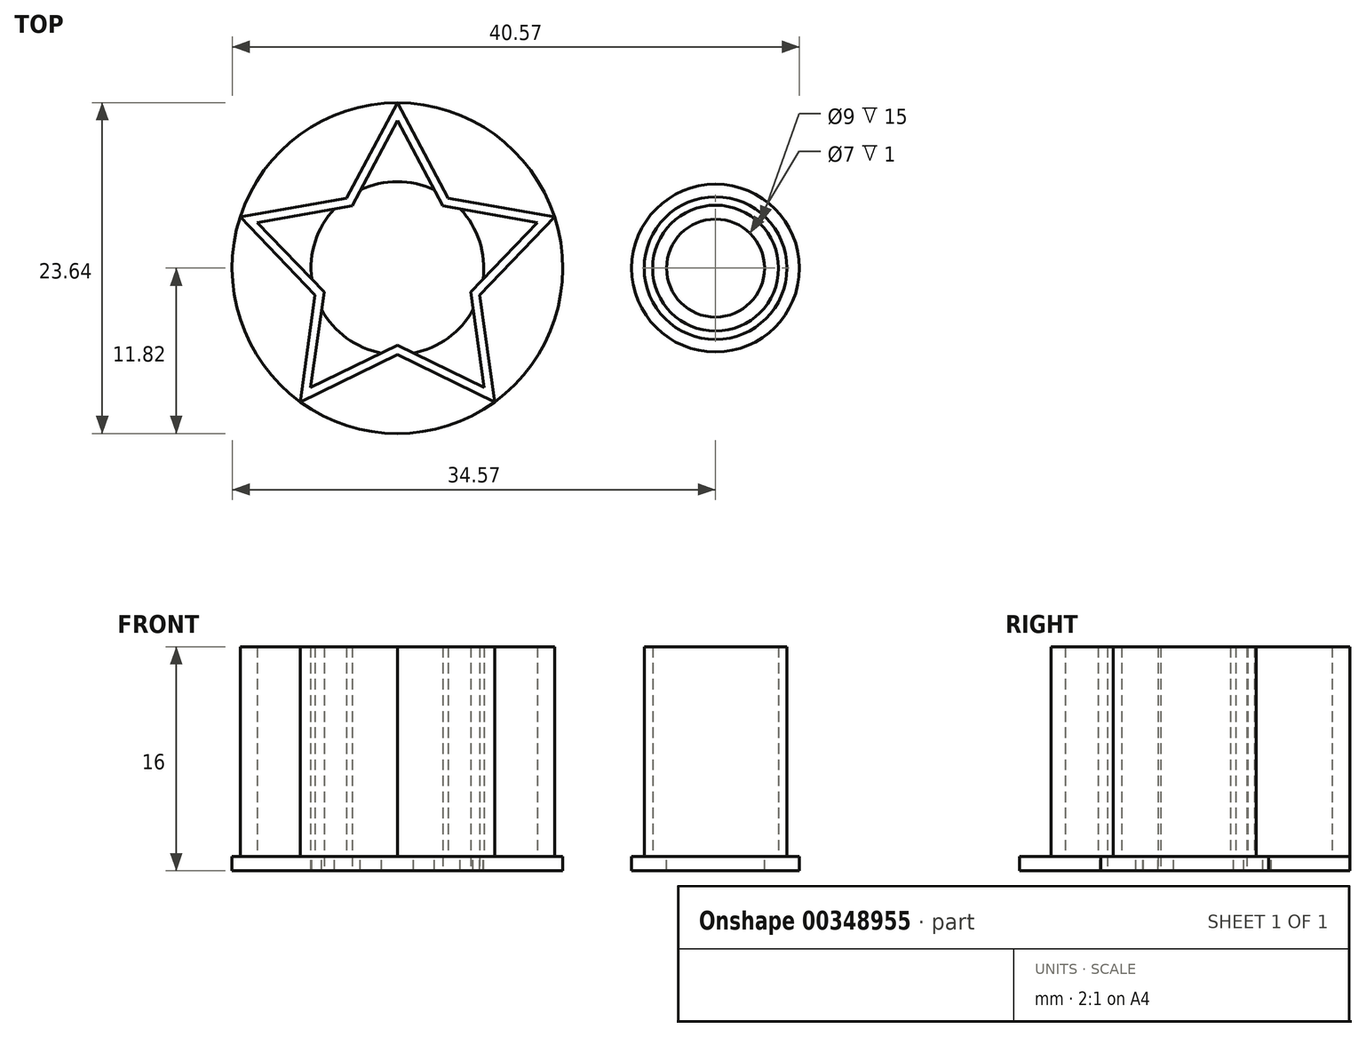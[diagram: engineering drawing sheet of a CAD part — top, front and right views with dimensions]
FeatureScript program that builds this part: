
annotation { "Feature Type Name" : "Feature", "Feature Type Description" : "" }
export const myFeature = defineFeature(function(context is Context, id is Id, definition is map)
    precondition{}
    {
        {
            var Q0;
            Q0=qCreatedBy(makeId("Top.planeOp"),FACE);
            var sketch = newSketch(context, id + "F0", { "sketchPlane" : qUnion([Q0])});
            skCircle(sketch, "E0", {"center": v(0, 0) * mm, "radius": 5.1 * mm});
            skCircle(sketch, "E1", {"center": v(0, 0) * mm, "radius": 4.5 * mm});
            skCircle(sketch, "E2", {"center": v(0, 0) * mm, "radius": 6 * mm});
            skCircle(sketch, "E3", {"center": v(0, 0) * mm, "radius": 3.5 * mm});
            skSolve(sketch);
        }
        {
            var Q0;
            Q0=makeQuery(id+"F0.imprint","IMPRINT",FACE,{"disambiguationData":[TD([[makeQuery(id+"F0.imprint","IMPRINT",EDGE,{"derivedFrom":sQuery(id+"F0.wireOp",EDGE,"E0")}),1.0]])]});
            extrude(context, id + "F1", {"entities" : qUnion([Q0]), "depth" : 15 * mm});
        }
        {
            var Q0;
            Q0=makeQuery(id+"F0.imprint","IMPRINT",FACE,{"disambiguationData":[TD([[makeQuery(id+"F0.imprint","IMPRINT",EDGE,{"derivedFrom":sQuery(id+"F0.wireOp",EDGE,"E0")}),-1.0]])]});
            var Q1;
            Q1=makeQuery(id+"F0.imprint","IMPRINT",FACE,{"disambiguationData":[TD([[makeQuery(id+"F0.imprint","IMPRINT",EDGE,{"derivedFrom":sQuery(id+"F0.wireOp",EDGE,"E1")}),1.0]])]});
            var Q2;
            Q2=makeQuery(id+"F0.imprint","IMPRINT",FACE,{"disambiguationData":[TD([[makeQuery(id+"F0.imprint","IMPRINT",EDGE,{"derivedFrom":sQuery(id+"F0.wireOp",EDGE,"E0")}),1.0]])]});
            extrude(context, id + "F2", {"entities" : qUnion([Q0, Q1, Q2]), "operationType" : NewBodyOperationType.ADD, "oppositeDirection" : true, "depth" : 1 * mm});
        }
        {
            var Q0;
            Q0=qCreatedBy(makeId("Top.planeOp"),FACE);
            var sketch = newSketch(context, id + "F3", { "sketchPlane" : qUnion([Q0])});
            skCircle(sketch, "E4.cCircle", {"center": v(-22.75, 0) * mm, "radius": 5 * mm, "construction": true});
            skLineSegment(sketch, "E4.0", {"start": v(-26.39, 5) * mm, "end": v(-19.12, 5) * mm});
            skLineSegment(sketch, "E4.1", {"start": v(-19.12, 5) * mm, "end": v(-16.88, -1.9) * mm});
            skLineSegment(sketch, "E4.2", {"start": v(-16.88, -1.9) * mm, "end": v(-22.75, -6.18) * mm});
            skLineSegment(sketch, "E4.3", {"start": v(-22.75, -6.18) * mm, "end": v(-28.63, -1.9) * mm});
            skLineSegment(sketch, "E4.4", {"start": v(-28.63, -1.9) * mm, "end": v(-26.39, 5) * mm});
            skPoint(sketch, "E4.0.midPoint", {"position": v(-22.75, 5) * mm});
            skLineSegment(sketch, "E5", {"start": v(-26.39, 5) * mm, "end": v(-34, 3.65) * mm});
            skLineSegment(sketch, "E6", {"start": v(-34, 3.65) * mm, "end": v(-28.63, -1.9) * mm});
            skLineSegment(sketch, "E7", {"start": v(-28.63, -1.9) * mm, "end": v(-29.7, -9.56) * mm});
            skLineSegment(sketch, "E8", {"start": v(-29.7, -9.56) * mm, "end": v(-22.75, -6.18) * mm});
            skLineSegment(sketch, "E9", {"start": v(-22.75, -6.18) * mm, "end": v(-15.8, -9.56) * mm});
            skLineSegment(sketch, "E10", {"start": v(-15.8, -9.56) * mm, "end": v(-16.88, -1.9) * mm});
            skLineSegment(sketch, "E11", {"start": v(-16.88, -1.9) * mm, "end": v(-11.51, 3.65) * mm});
            skLineSegment(sketch, "E12", {"start": v(-11.51, 3.65) * mm, "end": v(-19.12, 5) * mm});
            skLineSegment(sketch, "E13", {"start": v(-19.12, 5) * mm, "end": v(-22.75, 11.82) * mm});
            skLineSegment(sketch, "E14", {"start": v(-22.75, 11.82) * mm, "end": v(-26.39, 5) * mm});
            skSolve(sketch);
        }
        {
            var Q0;
            Q0 = qSketchRegion(id + "F3", true);
            extrude(context, id + "F4", {"entities" : qUnion([Q0]), "depth" : 15 * mm});
        }
        {
            var Q0;
            Q0=makeQuery(id+"F4.opExtrude","CAP_FACE",FACE,{"disambiguationData":[OSD([sQuery(id+"F3.wireOp",EDGE,"E5"),sQuery(id+"F3.wireOp",EDGE,"E6"),sQuery(id+"F3.wireOp",EDGE,"E7"),sQuery(id+"F3.wireOp",EDGE,"E8"),sQuery(id+"F3.wireOp",EDGE,"E9"),sQuery(id+"F3.wireOp",EDGE,"E10"),sQuery(id+"F3.wireOp",EDGE,"E11"),sQuery(id+"F3.wireOp",EDGE,"E12"),sQuery(id+"F3.wireOp",EDGE,"E13"),sQuery(id+"F3.wireOp",EDGE,"E14")])],"isStart":false});
            shell(context, id + "F5", {"entities" : qUnion([Q0]), "thickness" : 0.6 * mm});
        }
        {
            var Q0;
            Q0=makeQuery(id+"F5.opShell","OFFSET_FACE",FACE,{"disambiguationData":[OSD([sQuery(id+"F3.wireOp",EDGE,"E5"),sQuery(id+"F3.wireOp",EDGE,"E6"),sQuery(id+"F3.wireOp",EDGE,"E7"),sQuery(id+"F3.wireOp",EDGE,"E8"),sQuery(id+"F3.wireOp",EDGE,"E9"),sQuery(id+"F3.wireOp",EDGE,"E10"),sQuery(id+"F3.wireOp",EDGE,"E11"),sQuery(id+"F3.wireOp",EDGE,"E12"),sQuery(id+"F3.wireOp",EDGE,"E13"),sQuery(id+"F3.wireOp",EDGE,"E14")])]});
            extrude(context, id + "F6", {"entities" : qUnion([Q0]), "operationType" : NewBodyOperationType.REMOVE, "oppositeDirection" : true, "depth" : 25 * mm});
        }
        {
            var Q0;
            Q0=makeQuery(id+"F4.opExtrude","CAP_FACE",FACE,{"disambiguationData":[OSD([sQuery(id+"F3.wireOp",EDGE,"E5"),sQuery(id+"F3.wireOp",EDGE,"E6"),sQuery(id+"F3.wireOp",EDGE,"E7"),sQuery(id+"F3.wireOp",EDGE,"E8"),sQuery(id+"F3.wireOp",EDGE,"E9"),sQuery(id+"F3.wireOp",EDGE,"E10"),sQuery(id+"F3.wireOp",EDGE,"E11"),sQuery(id+"F3.wireOp",EDGE,"E12"),sQuery(id+"F3.wireOp",EDGE,"E13"),sQuery(id+"F3.wireOp",EDGE,"E14")])],"isStart":true});
            var sketch = newSketch(context, id + "F7", { "sketchPlane" : qUnion([Q0])});
            skCircle(sketch, "E15", {"center": v(-22.75, 0) * mm, "radius": 11.82 * mm});
            skCircle(sketch, "E16", {"center": v(-22.75, 0) * mm, "radius": 6.18 * mm});
            skSolve(sketch);
        }
        {
            var Q0;
            {var subQ7=makeQuery(id+"F4.opExtrude","CAP_EDGE",EDGE,{"disambiguationData":[OSD([sQuery(id+"F3.wireOp",EDGE,"E8")])],"isStart":true});Q0=makeQuery(id+"F7.imprint","IMPRINT",FACE,{"disambiguationData":[TD([[makeQuery(id+"F7.imprint","IMPRINT",EDGE,{"derivedFrom":subQ7}),1.0]])]});}
            var Q1;
            {var subQ0=sQuery(id+"F7.wireOp",EDGE,"E16");var subQ1=sQuery(id+"F3.wireOp",EDGE,"E10");var subQ2=sQuery(id+"F3.wireOp",EDGE,"E9");var subQ3=makeQuery(id+"F4.opExtrude","CAP_FACE",FACE,{"disambiguationData":[OSD([sQuery(id+"F3.wireOp",EDGE,"E5"),sQuery(id+"F3.wireOp",EDGE,"E6"),sQuery(id+"F3.wireOp",EDGE,"E7"),sQuery(id+"F3.wireOp",EDGE,"E8"),subQ2,subQ1,sQuery(id+"F3.wireOp",EDGE,"E11"),sQuery(id+"F3.wireOp",EDGE,"E12"),sQuery(id+"F3.wireOp",EDGE,"E13"),sQuery(id+"F3.wireOp",EDGE,"E14")])],"isStart":true});var subQ4=makeQuery(id+"F6.boolean.opBoolean","INTERSECT",EDGE,{"derivedFrom":[subQ3,makeQuery(id+"F6.opExtrude","SWEPT_FACE",FACE,{"disambiguationData":[OSD([subQ1])]})]});var subQ5=makeQuery(id+"F7.imprint","INTERSECT",VERTEX,{"derivedFrom":[subQ4,subQ0]});Q1=makeQuery(id+"F7.imprint","IMPRINT",FACE,{"disambiguationData":[TD([[makeQuery(id+"F7.imprint","IMPRINT",EDGE,{"disambiguationData":[TD([[subQ5,-1.0]])],"derivedFrom":subQ0}),-1.0]])]});}
            var Q2;
            {var subQ0=sQuery(id+"F7.wireOp",EDGE,"E16");var subQ1=sQuery(id+"F3.wireOp",EDGE,"E8");var subQ2=sQuery(id+"F3.wireOp",EDGE,"E7");var subQ3=makeQuery(id+"F4.opExtrude","CAP_FACE",FACE,{"disambiguationData":[OSD([sQuery(id+"F3.wireOp",EDGE,"E5"),sQuery(id+"F3.wireOp",EDGE,"E6"),subQ2,subQ1,sQuery(id+"F3.wireOp",EDGE,"E9"),sQuery(id+"F3.wireOp",EDGE,"E10"),sQuery(id+"F3.wireOp",EDGE,"E11"),sQuery(id+"F3.wireOp",EDGE,"E12"),sQuery(id+"F3.wireOp",EDGE,"E13"),sQuery(id+"F3.wireOp",EDGE,"E14")])],"isStart":true});var subQ4=makeQuery(id+"F6.boolean.opBoolean","INTERSECT",EDGE,{"derivedFrom":[subQ3,makeQuery(id+"F6.opExtrude","SWEPT_FACE",FACE,{"disambiguationData":[OSD([subQ1])]})]});var subQ5=makeQuery(id+"F7.imprint","INTERSECT",VERTEX,{"derivedFrom":[subQ4,subQ0]});Q2=makeQuery(id+"F7.imprint","IMPRINT",FACE,{"disambiguationData":[TD([[makeQuery(id+"F7.imprint","IMPRINT",EDGE,{"disambiguationData":[TD([[subQ5,-1.0]])],"derivedFrom":subQ0}),-1.0]])]});}
            var Q3;
            {var subQ0=sQuery(id+"F7.wireOp",EDGE,"E16");var subQ1=sQuery(id+"F3.wireOp",EDGE,"E6");var subQ2=sQuery(id+"F3.wireOp",EDGE,"E5");var subQ3=makeQuery(id+"F4.opExtrude","CAP_FACE",FACE,{"disambiguationData":[OSD([subQ2,subQ1,sQuery(id+"F3.wireOp",EDGE,"E7"),sQuery(id+"F3.wireOp",EDGE,"E8"),sQuery(id+"F3.wireOp",EDGE,"E9"),sQuery(id+"F3.wireOp",EDGE,"E10"),sQuery(id+"F3.wireOp",EDGE,"E11"),sQuery(id+"F3.wireOp",EDGE,"E12"),sQuery(id+"F3.wireOp",EDGE,"E13"),sQuery(id+"F3.wireOp",EDGE,"E14")])],"isStart":true});var subQ4=makeQuery(id+"F6.boolean.opBoolean","INTERSECT",EDGE,{"derivedFrom":[subQ3,makeQuery(id+"F6.opExtrude","SWEPT_FACE",FACE,{"disambiguationData":[OSD([subQ1])]})]});var subQ5=makeQuery(id+"F7.imprint","INTERSECT",VERTEX,{"derivedFrom":[subQ4,subQ0]});Q3=makeQuery(id+"F7.imprint","IMPRINT",FACE,{"disambiguationData":[TD([[makeQuery(id+"F7.imprint","IMPRINT",EDGE,{"disambiguationData":[TD([[subQ5,-1.0]])],"derivedFrom":subQ0}),-1.0]])]});}
            var Q4;
            {var subQ0=sQuery(id+"F7.wireOp",EDGE,"E16");var subQ1=sQuery(id+"F3.wireOp",EDGE,"E14");var subQ2=sQuery(id+"F3.wireOp",EDGE,"E13");var subQ3=makeQuery(id+"F4.opExtrude","CAP_FACE",FACE,{"disambiguationData":[OSD([sQuery(id+"F3.wireOp",EDGE,"E5"),sQuery(id+"F3.wireOp",EDGE,"E6"),sQuery(id+"F3.wireOp",EDGE,"E7"),sQuery(id+"F3.wireOp",EDGE,"E8"),sQuery(id+"F3.wireOp",EDGE,"E9"),sQuery(id+"F3.wireOp",EDGE,"E10"),sQuery(id+"F3.wireOp",EDGE,"E11"),sQuery(id+"F3.wireOp",EDGE,"E12"),subQ2,subQ1])],"isStart":true});var subQ4=makeQuery(id+"F6.boolean.opBoolean","INTERSECT",EDGE,{"derivedFrom":[subQ3,makeQuery(id+"F6.opExtrude","SWEPT_FACE",FACE,{"disambiguationData":[OSD([subQ1])]})]});var subQ5=makeQuery(id+"F7.imprint","INTERSECT",VERTEX,{"derivedFrom":[subQ4,subQ0]});Q4=makeQuery(id+"F7.imprint","IMPRINT",FACE,{"disambiguationData":[TD([[makeQuery(id+"F7.imprint","IMPRINT",EDGE,{"disambiguationData":[TD([[subQ5,-1.0]])],"derivedFrom":subQ0}),-1.0]])]});}
            var Q5;
            {var subQ0=sQuery(id+"F7.wireOp",EDGE,"E16");var subQ1=sQuery(id+"F3.wireOp",EDGE,"E11");var subQ2=sQuery(id+"F3.wireOp",EDGE,"E12");var subQ3=makeQuery(id+"F4.opExtrude","CAP_FACE",FACE,{"disambiguationData":[OSD([sQuery(id+"F3.wireOp",EDGE,"E5"),sQuery(id+"F3.wireOp",EDGE,"E6"),sQuery(id+"F3.wireOp",EDGE,"E7"),sQuery(id+"F3.wireOp",EDGE,"E8"),sQuery(id+"F3.wireOp",EDGE,"E9"),sQuery(id+"F3.wireOp",EDGE,"E10"),subQ1,subQ2,sQuery(id+"F3.wireOp",EDGE,"E13"),sQuery(id+"F3.wireOp",EDGE,"E14")])],"isStart":true});var subQ4=makeQuery(id+"F6.boolean.opBoolean","INTERSECT",EDGE,{"derivedFrom":[subQ3,makeQuery(id+"F6.opExtrude","SWEPT_FACE",FACE,{"disambiguationData":[OSD([subQ1])]})]});var subQ5=makeQuery(id+"F7.imprint","INTERSECT",VERTEX,{"derivedFrom":[subQ4,subQ0]});Q5=makeQuery(id+"F7.imprint","IMPRINT",FACE,{"disambiguationData":[TD([[makeQuery(id+"F7.imprint","IMPRINT",EDGE,{"disambiguationData":[TD([[subQ5,1.0]])],"derivedFrom":subQ0}),-1.0]])]});}
            var Q6;
            {var subQ0=sQuery(id+"F3.wireOp",EDGE,"E12");var subQ1=makeQuery(id+"F4.opExtrude","CAP_EDGE",EDGE,{"disambiguationData":[OSD([subQ0])],"isStart":true});Q6=makeQuery(id+"F7.imprint","IMPRINT",FACE,{"disambiguationData":[TD([[makeQuery(id+"F7.imprint","IMPRINT",EDGE,{"derivedFrom":subQ1}),-1.0]])]});}
            var Q7;
            {var subQ8=sQuery(id+"F3.wireOp",EDGE,"E7");var subQ24=makeQuery(id+"F4.opExtrude","CAP_EDGE",EDGE,{"disambiguationData":[OSD([subQ8])],"isStart":true});Q7=makeQuery(id+"F7.imprint","IMPRINT",FACE,{"disambiguationData":[TD([[makeQuery(id+"F7.imprint","IMPRINT",EDGE,{"derivedFrom":subQ24}),-1.0]])]});}
            var Q8;
            {var subQ0=sQuery(id+"F3.wireOp",EDGE,"E11");var subQ1=makeQuery(id+"F4.opExtrude","CAP_EDGE",EDGE,{"disambiguationData":[OSD([subQ0])],"isStart":true});var subQ2=sQuery(id+"F3.wireOp",EDGE,"E10");var subQ3=makeQuery(id+"F4.opExtrude","CAP_EDGE",EDGE,{"disambiguationData":[OSD([subQ2])],"isStart":true});var subQ4=makeQuery(id+"F7.imprint","INTERSECT",VERTEX,{"derivedFrom":[subQ3,subQ1]});Q8=makeQuery(id+"F7.imprint","IMPRINT",FACE,{"disambiguationData":[TD([[makeQuery(id+"F7.imprint","IMPRINT",EDGE,{"disambiguationData":[TD([[subQ4,1.0]])],"derivedFrom":subQ3}),-1.0]])]});}
            var Q9;
            {var subQ0=sQuery(id+"F7.wireOp",EDGE,"E16");var subQ1=sQuery(id+"F3.wireOp",EDGE,"E13");var subQ2=sQuery(id+"F3.wireOp",EDGE,"E12");var subQ3=makeQuery(id+"F7.imprint","INTERSECT",VERTEX,{"derivedFrom":[makeQuery(id+"F4.opExtrude","CAP_EDGE",EDGE,{"disambiguationData":[OSD([subQ2])],"isStart":true}),makeQuery(id+"F4.opExtrude","CAP_EDGE",EDGE,{"disambiguationData":[OSD([subQ1])],"isStart":true}),subQ0]});Q9=makeQuery(id+"F7.imprint","IMPRINT",FACE,{"disambiguationData":[TD([[makeQuery(id+"F7.imprint","IMPRINT",EDGE,{"disambiguationData":[TD([[subQ3,1.0]])],"derivedFrom":subQ0}),1.0]])]});}
            var Q10;
            {var subQ0=sQuery(id+"F7.wireOp",EDGE,"E16");var subQ1=sQuery(id+"F3.wireOp",EDGE,"E5");var subQ2=sQuery(id+"F3.wireOp",EDGE,"E14");var subQ3=makeQuery(id+"F4.opExtrude","CAP_FACE",FACE,{"disambiguationData":[OSD([subQ1,sQuery(id+"F3.wireOp",EDGE,"E6"),sQuery(id+"F3.wireOp",EDGE,"E7"),sQuery(id+"F3.wireOp",EDGE,"E8"),sQuery(id+"F3.wireOp",EDGE,"E9"),sQuery(id+"F3.wireOp",EDGE,"E10"),sQuery(id+"F3.wireOp",EDGE,"E11"),sQuery(id+"F3.wireOp",EDGE,"E12"),sQuery(id+"F3.wireOp",EDGE,"E13"),subQ2])],"isStart":true});var subQ4=makeQuery(id+"F6.boolean.opBoolean","INTERSECT",EDGE,{"derivedFrom":[subQ3,makeQuery(id+"F6.opExtrude","SWEPT_FACE",FACE,{"disambiguationData":[OSD([subQ1])]})]});var subQ5=makeQuery(id+"F7.imprint","INTERSECT",VERTEX,{"derivedFrom":[subQ4,subQ0]});Q10=makeQuery(id+"F7.imprint","IMPRINT",FACE,{"disambiguationData":[TD([[makeQuery(id+"F7.imprint","IMPRINT",EDGE,{"disambiguationData":[TD([[subQ5,-1.0]])],"derivedFrom":subQ0}),1.0]])]});}
            var Q11;
            {var subQ0=sQuery(id+"F7.wireOp",EDGE,"E16");var subQ1=sQuery(id+"F3.wireOp",EDGE,"E7");var subQ2=sQuery(id+"F3.wireOp",EDGE,"E6");var subQ3=makeQuery(id+"F4.opExtrude","CAP_FACE",FACE,{"disambiguationData":[OSD([sQuery(id+"F3.wireOp",EDGE,"E5"),subQ2,subQ1,sQuery(id+"F3.wireOp",EDGE,"E8"),sQuery(id+"F3.wireOp",EDGE,"E9"),sQuery(id+"F3.wireOp",EDGE,"E10"),sQuery(id+"F3.wireOp",EDGE,"E11"),sQuery(id+"F3.wireOp",EDGE,"E12"),sQuery(id+"F3.wireOp",EDGE,"E13"),sQuery(id+"F3.wireOp",EDGE,"E14")])],"isStart":true});var subQ4=makeQuery(id+"F6.boolean.opBoolean","INTERSECT",EDGE,{"derivedFrom":[subQ3,makeQuery(id+"F6.opExtrude","SWEPT_FACE",FACE,{"disambiguationData":[OSD([subQ1])]})]});var subQ5=makeQuery(id+"F7.imprint","INTERSECT",VERTEX,{"derivedFrom":[subQ4,subQ0]});Q11=makeQuery(id+"F7.imprint","IMPRINT",FACE,{"disambiguationData":[TD([[makeQuery(id+"F7.imprint","IMPRINT",EDGE,{"disambiguationData":[TD([[subQ5,-1.0]])],"derivedFrom":subQ0}),1.0]])]});}
            var Q12;
            {var subQ0=sQuery(id+"F7.wireOp",EDGE,"E16");var subQ1=sQuery(id+"F3.wireOp",EDGE,"E9");var subQ2=sQuery(id+"F3.wireOp",EDGE,"E8");var subQ3=makeQuery(id+"F4.opExtrude","CAP_FACE",FACE,{"disambiguationData":[OSD([sQuery(id+"F3.wireOp",EDGE,"E5"),sQuery(id+"F3.wireOp",EDGE,"E6"),sQuery(id+"F3.wireOp",EDGE,"E7"),subQ2,subQ1,sQuery(id+"F3.wireOp",EDGE,"E10"),sQuery(id+"F3.wireOp",EDGE,"E11"),sQuery(id+"F3.wireOp",EDGE,"E12"),sQuery(id+"F3.wireOp",EDGE,"E13"),sQuery(id+"F3.wireOp",EDGE,"E14")])],"isStart":true});var subQ4=makeQuery(id+"F6.boolean.opBoolean","INTERSECT",EDGE,{"derivedFrom":[subQ3,makeQuery(id+"F6.opExtrude","SWEPT_FACE",FACE,{"disambiguationData":[OSD([subQ1])]})]});var subQ5=makeQuery(id+"F7.imprint","INTERSECT",VERTEX,{"derivedFrom":[subQ4,subQ0]});Q12=makeQuery(id+"F7.imprint","IMPRINT",FACE,{"disambiguationData":[TD([[makeQuery(id+"F7.imprint","IMPRINT",EDGE,{"disambiguationData":[TD([[subQ5,-1.0]])],"derivedFrom":subQ0}),1.0]])]});}
            var Q13;
            {var subQ1=makeQuery(id+"F4.opExtrude","CAP_EDGE",EDGE,{"disambiguationData":[OSD([sQuery(id+"F3.wireOp",EDGE,"E7")])],"isStart":true});Q13=makeQuery(id+"F7.imprint","IMPRINT",FACE,{"disambiguationData":[TD([[makeQuery(id+"F7.imprint","IMPRINT",EDGE,{"derivedFrom":subQ1}),1.0]])]});}
            extrude(context, id + "F8", {"entities" : qUnion([Q0, Q1, Q2, Q3, Q4, Q5, Q6, Q7, Q8, Q9, Q10, Q11, Q12, Q13]), "operationType" : NewBodyOperationType.ADD, "depth" : 1 * mm});
        }
    });
